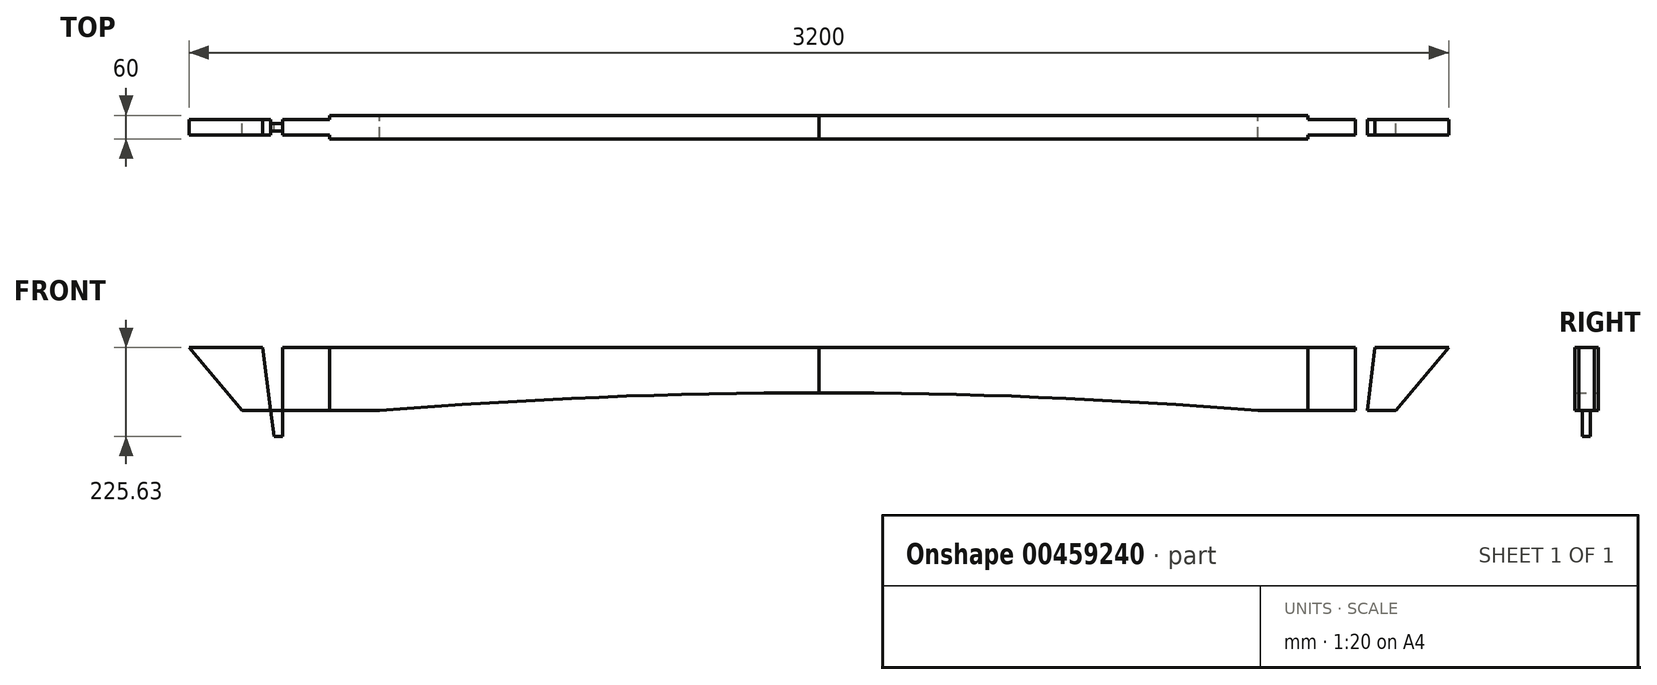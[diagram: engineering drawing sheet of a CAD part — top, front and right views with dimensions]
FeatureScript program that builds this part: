
annotation { "Feature Type Name" : "Feature", "Feature Type Description" : "" }
export const myFeature = defineFeature(function(context is Context, id is Id, definition is map)
    precondition{}
    {
        {
            var Q0;
            Q0=qCreatedBy(makeId("Front.planeOp"),FACE);
            var sketch = newSketch(context, id + "F0", { "sketchPlane" : qUnion([Q0])});
            skLineSegment(sketch, "E0", {"start": v(0, 0) * mm, "end": v(-1600, 0) * mm});
            skLineSegment(sketch, "E1", {"start": v(-1600, 0) * mm, "end": v(-1465.74, -160) * mm});
            skLineSegment(sketch, "E2", {"start": v(-1465.74, -160) * mm, "end": v(-1115.74, -160) * mm});
            skArc(sketch, "E3", {"start": v(0, -114.7) * mm, "mid": v(-558.33, -126.03) * mm, "end": v(-1115.74, -160) * mm});
            skLineSegment(sketch, "E4", {"start": v(0, -114.7) * mm, "end": v(-352.96, -114.7) * mm, "construction": true});
            skLineSegment(sketch, "E5", {"start": v(0, 0) * mm, "end": v(0, -308.33) * mm, "construction": true});
            skLineSegment(sketch, "E6.bottom", {"start": v(-1412.8, 0) * mm, "end": v(-1362.8, 0) * mm});
            skLineSegment(sketch, "E6.right", {"start": v(-1362.8, 0) * mm, "end": v(-1362.8, -160) * mm});
            skLineSegment(sketch, "E7", {"start": v(-1242.8, -160) * mm, "end": v(-1242.8, 0) * mm});
            skLineSegment(sketch, "E8", {"start": v(-1412.8, 0) * mm, "end": v(-1392.8, -160) * mm});
            skLineSegment(sketch, "E9", {"start": v(-1412.8, 0) * mm, "end": v(-1420.38, 60.65) * mm});
            skLineSegment(sketch, "E10", {"start": v(-1420.38, 60.65) * mm, "end": v(-1362.8, 60.65) * mm});
            skLineSegment(sketch, "E11", {"start": v(-1362.8, 60.65) * mm, "end": v(-1362.8, 0) * mm});
            skLineSegment(sketch, "E12", {"start": v(-1392.8, -160) * mm, "end": v(-1384.6, -225.63) * mm});
            skLineSegment(sketch, "E13", {"start": v(-1384.6, -225.63) * mm, "end": v(-1362.8, -225.63) * mm});
            skLineSegment(sketch, "E14", {"start": v(-1362.8, -225.63) * mm, "end": v(-1362.8, -160) * mm});
            skLineSegment(sketch, "E15", {"start": v(0, -114.7) * mm, "end": v(0, 0) * mm});
            skSolve(sketch);
        }
        {
            var Q0;
            {var subQ0=sQuery(id+"F0.wireOp",EDGE,"E1");Q0=makeQuery(id+"F0.imprint","IMPRINT",FACE,{"disambiguationData":[TD([[makeQuery(id+"F0.imprint","IMPRINT",EDGE,{"derivedFrom":subQ0}),1.0]])]});}
            var Q1;
            {var subQ0=sQuery(id+"F0.wireOp",EDGE,"E6.right");Q1=makeQuery(id+"F0.imprint","IMPRINT",FACE,{"disambiguationData":[TD([[makeQuery(id+"F0.imprint","IMPRINT",EDGE,{"derivedFrom":subQ0}),1.0]])]});}
            var Q2;
            Q2=makeQuery(id+"F0.imprint","IMPRINT",FACE,{"disambiguationData":[TD([[makeQuery(id+"F0.imprint","IMPRINT",EDGE,{"derivedFrom":sQuery(id+"F0.wireOp",EDGE,"E6.bottom")}),-1.0]])]});
            extrude(context, id + "F1", {"entities" : qUnion([Q0, Q1, Q2]), "endBound" : BoundingType.SYMMETRIC, "depth" : 40 * mm});
        }
        {
            var Q0;
            Q0=makeQuery(id+"F0.imprint","IMPRINT",FACE,{"disambiguationData":[TD([[makeQuery(id+"F0.imprint","IMPRINT",EDGE,{"derivedFrom":sQuery(id+"F0.wireOp",EDGE,"E6.bottom")}),-1.0]])]});
            var Q1;
            Q1=makeQuery(id+"F0.imprint","IMPRINT",FACE,{"disambiguationData":[TD([[makeQuery(id+"F0.imprint","IMPRINT",EDGE,{"derivedFrom":sQuery(id+"F0.wireOp",EDGE,"E6.bottom")}),1.0]])]});
            var Q2;
            {var subQ2=sQuery(id+"F0.wireOp",EDGE,"E12");Q2=makeQuery(id+"F0.imprint","IMPRINT",FACE,{"disambiguationData":[TD([[makeQuery(id+"F0.imprint","IMPRINT",EDGE,{"derivedFrom":subQ2}),1.0]])]});}
            extrude(context, id + "F2", {"entities" : qUnion([Q0, Q1, Q2]), "endBound" : BoundingType.SYMMETRIC, "depth" : 20 * mm});
        }
        {
            var Q0;
            Q0=makeQuery(id+"F2.opExtrude","SWEPT_BODY",BODY,{"disambiguationData":[OSD([sQuery(id+"F0.wireOp",EDGE,"E6.right"),sQuery(id+"F0.wireOp",EDGE,"E8"),sQuery(id+"F0.wireOp",EDGE,"E9"),sQuery(id+"F0.wireOp",EDGE,"E10"),sQuery(id+"F0.wireOp",EDGE,"E11"),sQuery(id+"F0.wireOp",EDGE,"E12"),sQuery(id+"F0.wireOp",EDGE,"E13"),sQuery(id+"F0.wireOp",EDGE,"E14")])]});
            var Q1;
            Q1=makeQuery(id+"F1.opExtrude","SWEPT_BODY",BODY,{"disambiguationData":[OSD([sQuery(id+"F0.wireOp",EDGE,"E0"),sQuery(id+"F0.wireOp",EDGE,"E1"),sQuery(id+"F0.wireOp",EDGE,"E2"),sQuery(id+"F0.wireOp",EDGE,"E3"),sQuery(id+"F0.wireOp",EDGE,"9c49f7a9-e606-4a53-a230-6eb055f8ba8b0.MirrorCS"),sQuery(id+"F0.wireOp",EDGE,"9c49f7a9-e606-4a53-a230-6eb055f8ba8b1.MirrorCS"),sQuery(id+"F0.wireOp",EDGE,"9c49f7a9-e606-4a53-a230-6eb055f8ba8b3.MirrorCS"),sQuery(id+"F0.wireOp",EDGE,"9c49f7a9-e606-4a53-a230-6eb055f8ba8b4.MirrorCS"),sQuery(id+"F0.wireOp",EDGE,"E6.bottom")])]});
            booleanBodies(context, id + "F3", {"operationType" : BooleanOperationType.SUBTRACTION, "tools" : qUnion([Q0]), "targets" : qUnion([Q1]), "keepTools" : true});
        }
        {
            var Q0;
            {var subQ1=sQuery(id+"F0.wireOp",EDGE,"E3");Q0=makeQuery(id+"F0.imprint","IMPRINT",FACE,{"disambiguationData":[TD([[makeQuery(id+"F0.imprint","IMPRINT",EDGE,{"derivedFrom":subQ1}),-1.0]])]});}
            extrude(context, id + "F4", {"entities" : qUnion([Q0]), "operationType" : NewBodyOperationType.ADD, "endBound" : BoundingType.SYMMETRIC, "depth" : 60 * mm});
        }
        {
            var Q0;
            Q0=makeQuery(id+"F1.opExtrude","SWEPT_BODY",BODY,{"disambiguationData":[OSD([sQuery(id+"F0.wireOp",EDGE,"E0"),sQuery(id+"F0.wireOp",EDGE,"E1"),sQuery(id+"F0.wireOp",EDGE,"E2"),sQuery(id+"F0.wireOp",EDGE,"E6.bottom"),sQuery(id+"F0.wireOp",EDGE,"E7")])]});
            var Q1;
            Q1=qCreatedBy(makeId("Right.planeOp"),FACE);
            mirror(context, id + "F5", {"operationType" : NewBodyOperationType.ADD, "entities" : qUnion([Q0]), "mirrorPlane" : qUnion([Q1])});
        }
    });
